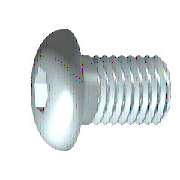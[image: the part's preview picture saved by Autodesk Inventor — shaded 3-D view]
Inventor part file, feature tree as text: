
AUTODESK INVENTOR PART (.ipt)
format: ipt  version: 2024.2 (Build 282272000, 272)  size: 205,824 bytes
history: native  units: mm (DEFAULTED — no unit token found)
features: extrude x1, plane x1, fillet x1
ambient origin geometry x7: Origin, YZ Plane, XY Plane, X Axis, Y Axis, Z Axis, Center Point
bodies: Solid1 (feature_tree), Body (feature_tree)
feature tree (3):
  extrude  "Slot"  Depth=7.0mm
  plane  "Work Plane1"
  fillet  "Fillet2"  Radius=0.61355mm
